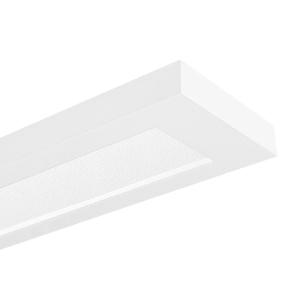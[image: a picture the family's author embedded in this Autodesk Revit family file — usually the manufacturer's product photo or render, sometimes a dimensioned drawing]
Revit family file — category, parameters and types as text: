
# Revit family: 3f_filippi_-_3f_travetta_di_lgs_3f_filippi_-_11629_-_3f_travetta_led_di_2x22w_dali_lgs_l1590
name_source: partatom
category: Lighting Fixtures
units: mm (PartAtom-declared; Revit-internal decimal feet)

## family parameters
Cut with Voids When Loaded = No
Host = Face
Light Source = No
Part Type = Normal
Room Calculation Point = No
Round Connector Dimension = Use Diameter
Shared = No

## types (1)
- 3F Filippi - 3F Travetta DI LGS (1 x LED, 5096 lm, 49 W, 4000 K)
    Apparent Load = 49 VA
    Approval mark = ENEC
    CIE Flux Codes = 64 93 99 85 100
    Color Rendering = 80
    Color Temperature = 4000 K
    Control Gear = Electronic transformer
    Default Elevation = 1800 mm
    Description = ILLUMINOTECHNICAL
Luminous efficiency 100% (DLOR 85%, ULOR 15%).
Initial luminous flux of the luminaire 5096 lm.
Symmetric direct-indirect distribution.
Installation Interdistance Transv.D = 1.18 x hu - Long.D = 1.18 x hu.
Average luminance <3000 cd/m² for radial angles >65°.
Tabular UGR (CIE 117 - 4H-8H; S=0.25H; 70/50/20): RUG 17.2 - 17.8.
Beam angle: 89° - 91°.
Luminous efficacy 104 lm/W.
Lifetime (L93/B10): 30000 h. (tq+25°C)
Lifetime (L90/B10): 50000 h. (tq+25°C)
Lifetime (L85/B10): 80000 h. (tq+25°C)
Lifetime (L80/B10): 100000 h. (tq+25°C)
Sudden decreased luminous flux after 50000 hours: 0% (C0).
Photobiological safety in compliance with IEC/TR 62778: RG0 risk exempt, (IEC 62471).
In compliance with IEC/EN 62722-2-1 - IEC/EN 62717 standards.

SOURCE
2 linear LED modules 22W/840.
Energy efficiency class (UE 2019/2020 - UE 2019/2015): D.
CIE 13.3 Colour rendering index: CRI >80 (R9 <50%).
IES TM-30 Fidelity Index: Rf = 84 Rg = 95.
CCT nominal colour temperature 4000 K.
Colour initial tolerance (MacAdam): SDCM 2.

MECHANICAL
Housing with squared shape in white painted galvannealed steel, with nonreflecting surface.
Flow recuperator in semi-glossy aluminium.
LGS micro-prismatic flat diffuser in transparent methacrylate (PMMA), multi-lenticular exterior, anti-glare.
Anti-glare opal polycarbonate filter for brightness uniformity.
Upper holes closing film made of opal polycarbonate.
Luminaire with limited surface temperature. - D - (EN 60598-2-24)
Dimensions: 1590x190 mm, height 60 mm. Weight 5.6 kg.
IP20 protection degree.
Glow-wire test resistance 650°C.

ELECTRICAL
Halogen Free DALI-2 DATI (Parts 251, 252, 253), PUSH-DIM, electronic wiring 230V-50/60Hz, power factor 0.95 at full load, THD <25%, constant output current, SELV, class I, 1 driver, 1 DALI addresse.
Power of the luminaire 49 W.
CE - IEC 60598-1 - EN 60598-1.
SAFE FLICKER: PstLM=<1 and SVM=<0.4 (IEC TR 61547-1 and IEC TR 63158), to ensure a more comfortable and safe light.
Luminaire compliant with EN 60598-2-22 for power supply from a centralised emergency system CPSS (Central Power Supply System), not incorporated in the luminaire - high risk areas excluded. The default power and flux are 100% in AC and 15% in DC.
Ambient temperature from 0°C to +25°C.
Temperature class T6 max 85°C.
Relative humidity UR: <85%.

INSTALLATION
Suspended.
All accessories dedicated to this product are available on the Catalog and on our website www.3F-Filippi.com.

APPLICATIONS
In environments, even with reduced height, requiring a comfortable light.
In environments with VDTs, managerial offices and staterooms, public offices and schools.

LIGHT MANAGEMENT
Recommended minimum setting: 10%.
The luminaire, equipped with (DALI-2 DATI) driver, can be controlled manually with 3F Easy Dim technology or automatically/manually with wired or wireless DALI/D2D control systems.
The D2D driver guarantees interoperability with other devices with the same certification by making the following information available:
Device Data (Part 251), Energy Report (Part 252), Diagnosis & Maintenance (Part 253).
In electrical systems without a regulation system (manual or automatic) and DALI bus, a suitable jumper must be made on the DA-DA terminals of the appliance.

WARNING
Luminaire designed for disposal/recycling at end-of-life.
Replaceable (LED only) light source by a professional. Replaceable control gear by a professional.
    Height = 60 mm  [stored 0.19685 ft]
    Lamp = 1 x LED
    Lamp Light Flux = 5096 lm
    Lamp Power = 49 W
    Lamp count = 1
    Length = 1590 mm
    Lifetime = 50000 h
    Luminous efficacy = 104 lm/W
    Manufacturer = 3F Filippi
    ModVariant = No
    Model = 3F Filippi - 11629 - 3F Travetta LED DI 2x22W DALI LGS L1590
    Mounting Place = Ceiling
    Mounting Type = Pendant
    Number of Poles = 1
    OnlyDefault = Yes
    Power Factor = 1
    Product Name = 3F Filippi - 3F Travetta DI LGS
    Product group = pendant luminaire
    ProductGroupID = 9
    Protection Class = Protection class I
    Protection Degree = IP 20
    RLX_Detail_Level = 1
    RLX_Emergency_Light_Flux = 0 lm
    RLX_Emergency_Type = 0
    RLX_Emergency_Type_DB = No
    RlxData = <blob elided: 52657 chars, md5=659a3828>
    Socket = socket
    Standby Power = 0 W
    System Light Flux = 5096 lm
    System Power = 49 W
    Type Comments = Product without accessories
    Type Image = 3ffilippi_3f_travetta_led_lgs.jpg
    URL = http://relux.com
    VarID = ---
    Voltage = 0 V
    Weight = 0.00 kg
    Width = 190 mm  [stored 0.62336 ft]

note: [stored X ft] marks values corroborated as IEEE doubles in the binary element streams (Revit-internal decimal feet)

## geometry (parser evidence)
native form markers: Blend x4, Sweep x15
no freeform markers — native parametric forms only
